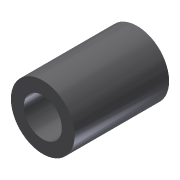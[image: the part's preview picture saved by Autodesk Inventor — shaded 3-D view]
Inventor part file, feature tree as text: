
AUTODESK INVENTOR PART (.ipt)
format: ipt  version: 2013 (Build 170138000, 138)  size: 81,408 bytes
history: native  units: in
note: dims shown in document units (in); Inventor stores cm internally (conversion verified against a paired STEP export)
features: extrude x1, sketch x1
ambient origin geometry x8: Origin, YZ Plane, XZ Plane, XY Plane, X Axis, Y Axis, Z Axis, Center Point
bodies: Solid1 (feature_tree)
feature tree (2):
  extrude  "Extrusion1"  Depth=0.675in
  sketch  "Sketch1"  dims[d0=0.403in d2=0.675in d3=1.0in d4=0.0in]
